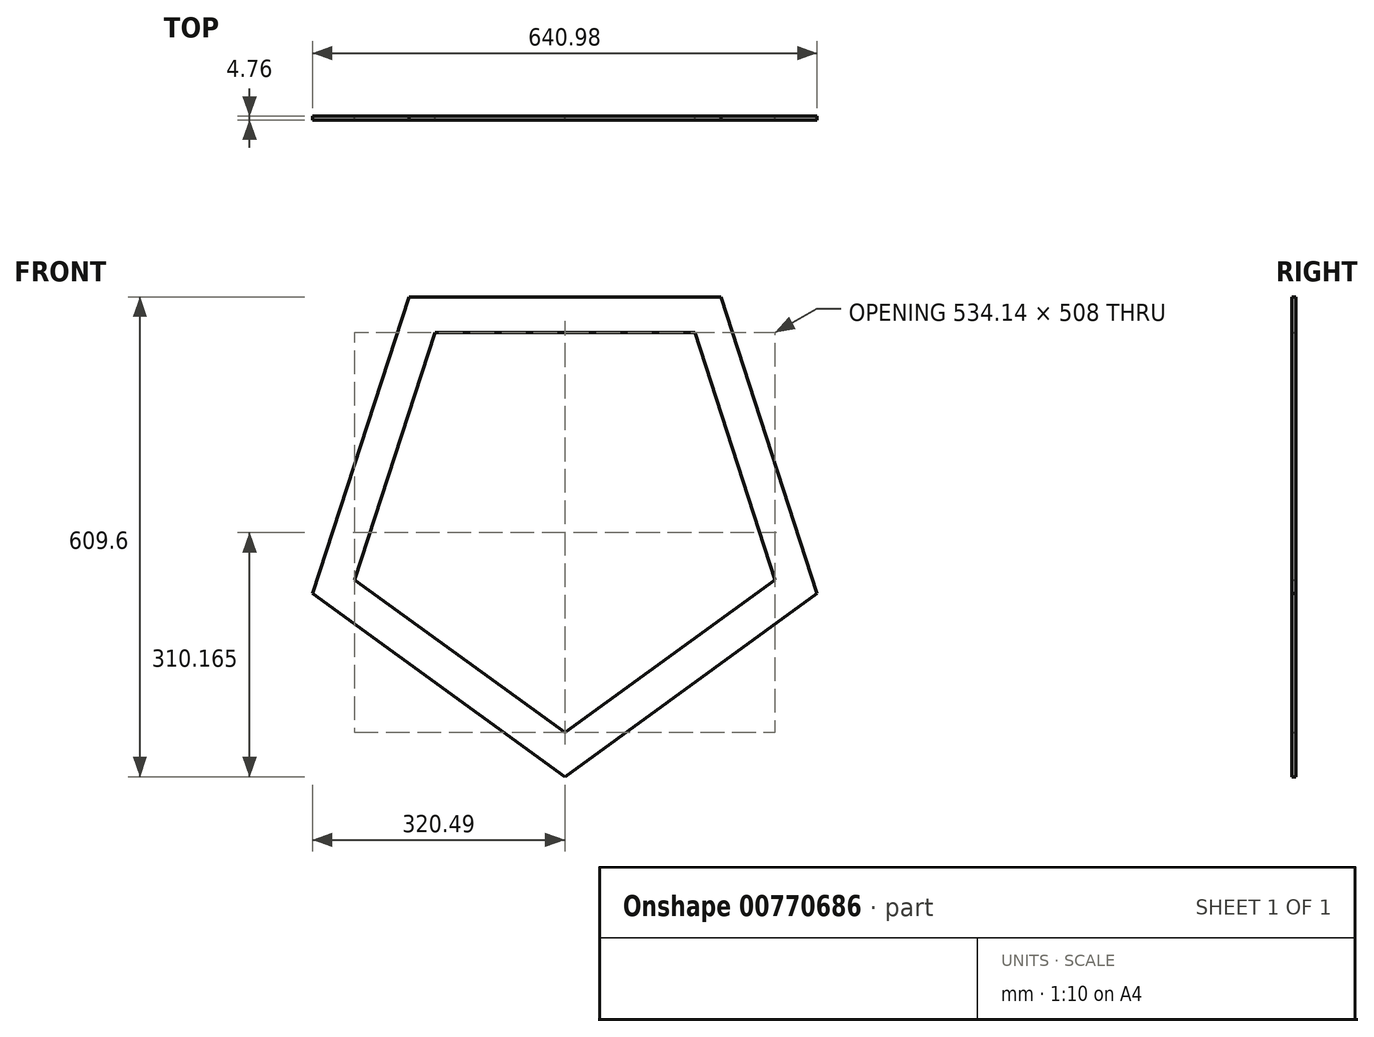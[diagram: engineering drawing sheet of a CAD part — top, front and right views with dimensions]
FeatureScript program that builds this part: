
annotation { "Feature Type Name" : "Feature", "Feature Type Description" : "" }
export const myFeature = defineFeature(function(context is Context, id is Id, definition is map)
    precondition{}
    {
        {
            var Q0;
            Q0=qCreatedBy(makeId("Front.planeOp"),FACE);
            var sketch = newSketch(context, id + "F0", { "sketchPlane" : qUnion([Q0])});
            skCircle(sketch, "E0.cCircle", {"center": v(0, 0) * mm, "radius": 272.62 * mm, "construction": true});
            skLineSegment(sketch, "E0.0", {"start": v(-198.07, 272.62) * mm, "end": v(198.07, 272.62) * mm});
            skLineSegment(sketch, "E0.1", {"start": v(198.07, 272.62) * mm, "end": v(320.49, -104.13) * mm});
            skLineSegment(sketch, "E0.2", {"start": v(320.49, -104.13) * mm, "end": v(0, -336.98) * mm});
            skLineSegment(sketch, "E0.3", {"start": v(0, -336.98) * mm, "end": v(-320.49, -104.13) * mm});
            skLineSegment(sketch, "E0.4", {"start": v(-320.49, -104.13) * mm, "end": v(-198.07, 272.62) * mm});
            skPoint(sketch, "E0.0.midPoint", {"position": v(0, 272.62) * mm});
            skCircle(sketch, "E1.cCircle", {"center": v(0, 0) * mm, "radius": 227.18 * mm, "construction": true});
            skLineSegment(sketch, "E1.0", {"start": v(-165.06, 227.18) * mm, "end": v(165.06, 227.18) * mm});
            skLineSegment(sketch, "E1.1", {"start": v(165.06, 227.18) * mm, "end": v(267.07, -86.78) * mm});
            skLineSegment(sketch, "E1.2", {"start": v(267.07, -86.78) * mm, "end": v(0, -280.82) * mm});
            skLineSegment(sketch, "E1.3", {"start": v(0, -280.82) * mm, "end": v(-267.07, -86.78) * mm});
            skLineSegment(sketch, "E1.4", {"start": v(-267.07, -86.78) * mm, "end": v(-165.06, 227.18) * mm});
            skPoint(sketch, "E1.0.midPoint", {"position": v(0, 227.18) * mm});
            skSolve(sketch);
        }
        {
            var Q0;
            Q0 = qSketchRegion(id + "F0", true);
            extrude(context, id + "F1", {"entities" : qUnion([Q0]), "endBound" : BoundingType.SYMMETRIC, "depth" : 4.76 * mm, "offsetDistance" : 25.4 * mm});
        }
    });
